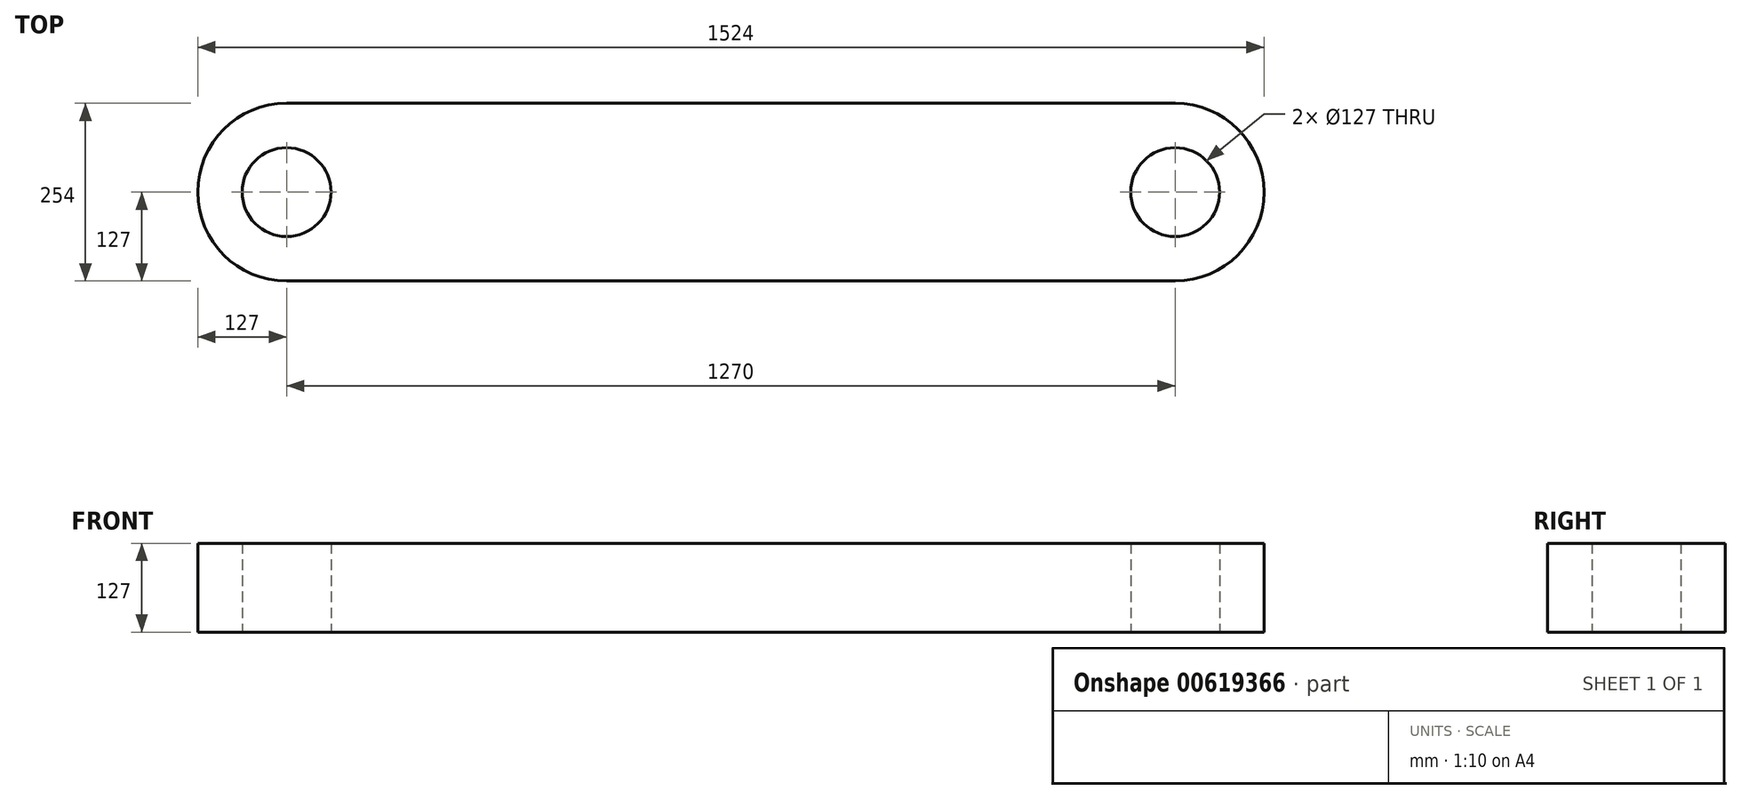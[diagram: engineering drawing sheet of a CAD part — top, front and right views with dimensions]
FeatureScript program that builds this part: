
annotation { "Feature Type Name" : "Feature", "Feature Type Description" : "" }
export const myFeature = defineFeature(function(context is Context, id is Id, definition is map)
    precondition{}
    {
        {
            var Q0;
            Q0=qCreatedBy(makeId("Top.planeOp"),FACE);
            var sketch = newSketch(context, id + "F0", { "sketchPlane" : qUnion([Q0])});
            skLineSegment(sketch, "E0.bottom", {"start": v(-1270, 127) * mm, "end": v(0, 127) * mm});
            skLineSegment(sketch, "E0.top", {"start": v(-1270, -127) * mm, "end": v(0, -127) * mm});
            skArc(sketch, "E1", {"start": v(0, -127) * mm, "mid": v(127, 0) * mm, "end": v(0, 127) * mm});
            skArc(sketch, "E2", {"start": v(-1270, 127) * mm, "mid": v(-1397, 0) * mm, "end": v(-1270, -127) * mm});
            skCircle(sketch, "E3", {"center": v(-1270, 0) * mm, "radius": 63.5 * mm});
            skCircle(sketch, "E4", {"center": v(0, 0) * mm, "radius": 63.5 * mm});
            skSolve(sketch);
        }
        {
            var Q0;
            Q0 = qSketchRegion(id + "F0", true);
            extrude(context, id + "F1", {"entities" : qUnion([Q0]), "depth" : 127 * mm, "offsetDistance" : 25.4 * mm});
        }
    });
